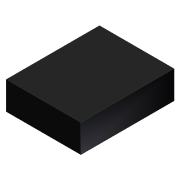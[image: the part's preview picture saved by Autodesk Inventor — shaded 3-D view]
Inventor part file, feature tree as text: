
AUTODESK INVENTOR PART (.ipt)
format: ipt  version: unknown  size: 165,376 bytes
history: native  units: mm
features: extrude x1, sketch x1
ambient origin geometry x8: Origin, YZ Plane, XZ Plane, XY Plane, X Axis, Y Axis, Z Axis, Center Point
feature tree (2):
  extrude  "Выдавливание2"  Depth=4.0mm
  sketch  "Эскиз2"
